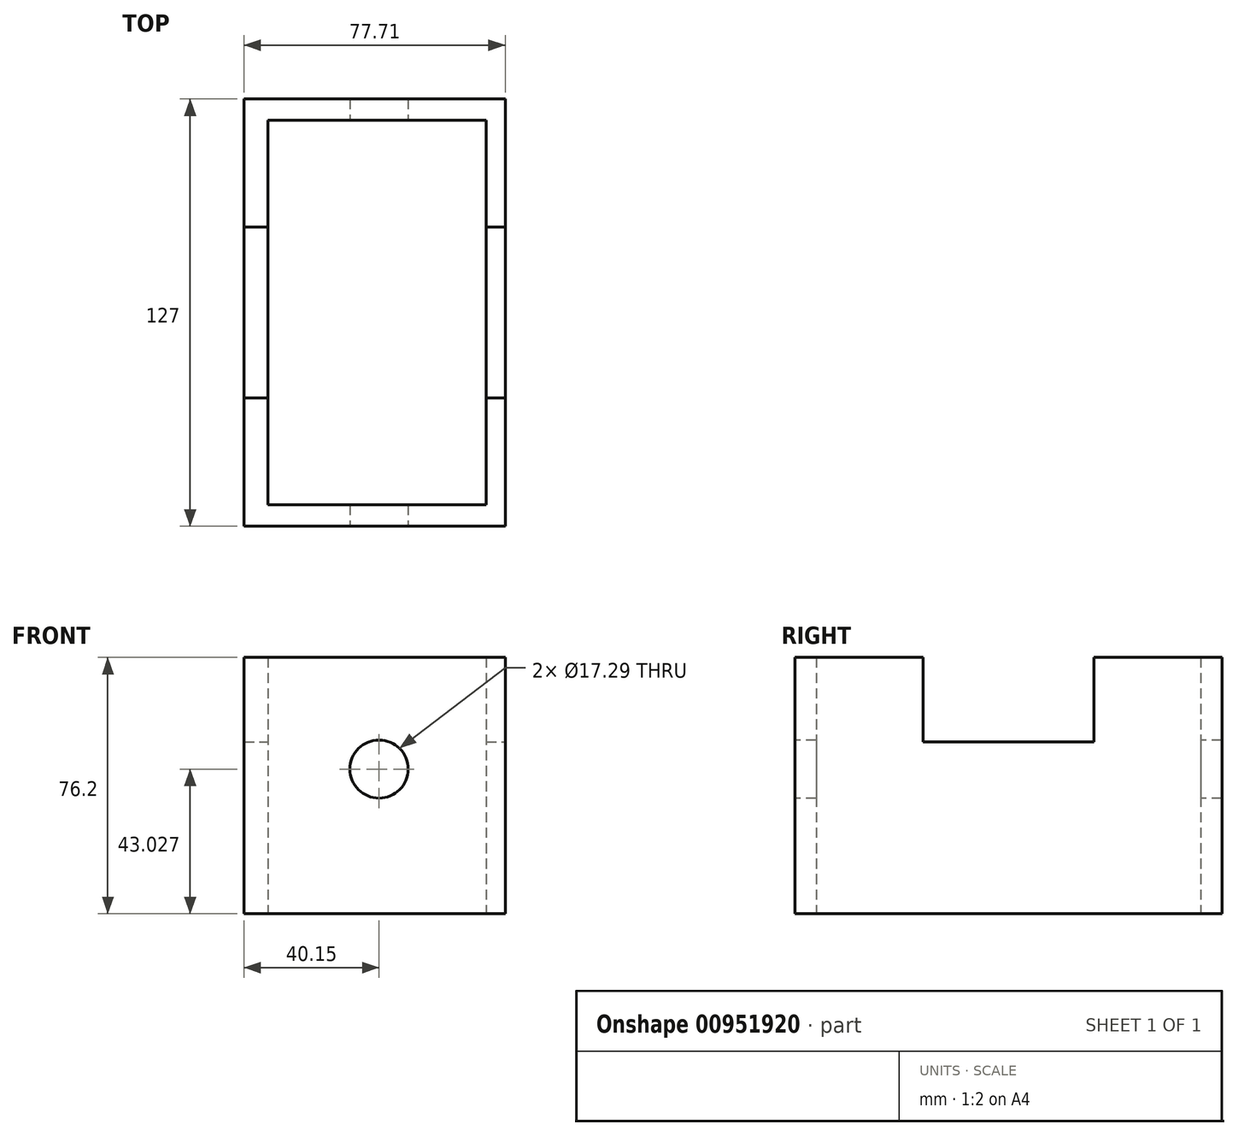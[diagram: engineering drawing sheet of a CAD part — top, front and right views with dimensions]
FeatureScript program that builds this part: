
annotation { "Feature Type Name" : "Feature", "Feature Type Description" : "" }
export const myFeature = defineFeature(function(context is Context, id is Id, definition is map)
    precondition{}
    {
        {
            var Q0;
            Q0=qCreatedBy(makeId("Top.planeOp"),FACE);
            var sketch = newSketch(context, id + "F0", { "sketchPlane" : qUnion([Q0])});
            skLineSegment(sketch, "E0.bottom", {"start": v(-40.15, 63.5) * mm, "end": v(37.56, 63.5) * mm});
            skLineSegment(sketch, "E0.top", {"start": v(-40.15, -63.5) * mm, "end": v(37.56, -63.5) * mm});
            skLineSegment(sketch, "E0.left", {"start": v(-40.15, 63.5) * mm, "end": v(-40.15, -63.5) * mm});
            skLineSegment(sketch, "E0.right", {"start": v(37.56, 63.5) * mm, "end": v(37.56, -63.5) * mm});
            skSolve(sketch);
        }
        {
            var Q0;
            Q0=makeQuery(id+"F0.imprint","IMPRINT",FACE,{"disambiguationData":[TD([[makeQuery(id+"F0.imprint","IMPRINT",EDGE,{"derivedFrom":sQuery(id+"F0.wireOp",EDGE,"E0.bottom")}),-1.0]])]});
            extrude(context, id + "F1", {"entities" : qUnion([Q0]), "depth" : 76.2 * mm, "offsetDistance" : 25.4 * mm});
        }
        {
            var Q0;
            Q0=qCreatedBy(makeId("Top.planeOp"),FACE);
            var sketch = newSketch(context, id + "F2", { "sketchPlane" : qUnion([Q0])});
            skLineSegment(sketch, "E1.bottom", {"start": v(-33, 57.15) * mm, "end": v(31.85, 57.15) * mm});
            skLineSegment(sketch, "E1.top", {"start": v(-33, -57.15) * mm, "end": v(31.85, -57.15) * mm});
            skLineSegment(sketch, "E1.left", {"start": v(-33, 57.15) * mm, "end": v(-33, -57.15) * mm});
            skLineSegment(sketch, "E1.right", {"start": v(31.85, 57.15) * mm, "end": v(31.85, -57.15) * mm});
            skSolve(sketch);
        }
        {
            var Q0;
            Q0 = qSketchRegion(id + "F2", true);
            extrude(context, id + "F3", {"entities" : qUnion([Q0]), "operationType" : NewBodyOperationType.REMOVE, "depth" : 123.44 * mm, "offsetDistance" : 25.4 * mm});
        }
        {
            var Q0;
            Q0=qCreatedBy(makeId("Front.planeOp"),FACE);
            var sketch = newSketch(context, id + "F4", { "sketchPlane" : qUnion([Q0])});
            skCircle(sketch, "E2", {"center": v(0, 43.03) * mm, "radius": 8.64 * mm});
            skSolve(sketch);
        }
        {
            var Q0;
            Q0 = qSketchRegion(id + "F4", true);
            extrude(context, id + "F5", {"entities" : qUnion([Q0]), "operationType" : NewBodyOperationType.REMOVE, "oppositeDirection" : true, "depth" : 232.16 * mm, "offsetDistance" : 25.4 * mm, "symmetric" : true});
        }
        {
            var Q0;
            Q0=qCreatedBy(makeId("Right.planeOp"),FACE);
            var sketch = newSketch(context, id + "F6", { "sketchPlane" : qUnion([Q0])});
            skLineSegment(sketch, "E3.bottom", {"start": v(25.4, 76.41) * mm, "end": v(-25.4, 76.41) * mm});
            skLineSegment(sketch, "E3.top", {"start": v(25.4, 51.09) * mm, "end": v(-25.4, 51.09) * mm});
            skLineSegment(sketch, "E3.left", {"start": v(25.4, 76.41) * mm, "end": v(25.4, 51.09) * mm});
            skLineSegment(sketch, "E3.right", {"start": v(-25.4, 76.41) * mm, "end": v(-25.4, 51.09) * mm});
            skSolve(sketch);
        }
        {
            var Q0;
            Q0 = qSketchRegion(id + "F6", true);
            extrude(context, id + "F7", {"entities" : qUnion([Q0]), "operationType" : NewBodyOperationType.REMOVE, "oppositeDirection" : true, "depth" : 117.35 * mm, "offsetDistance" : 25.4 * mm, "symmetric" : true});
        }
    });
